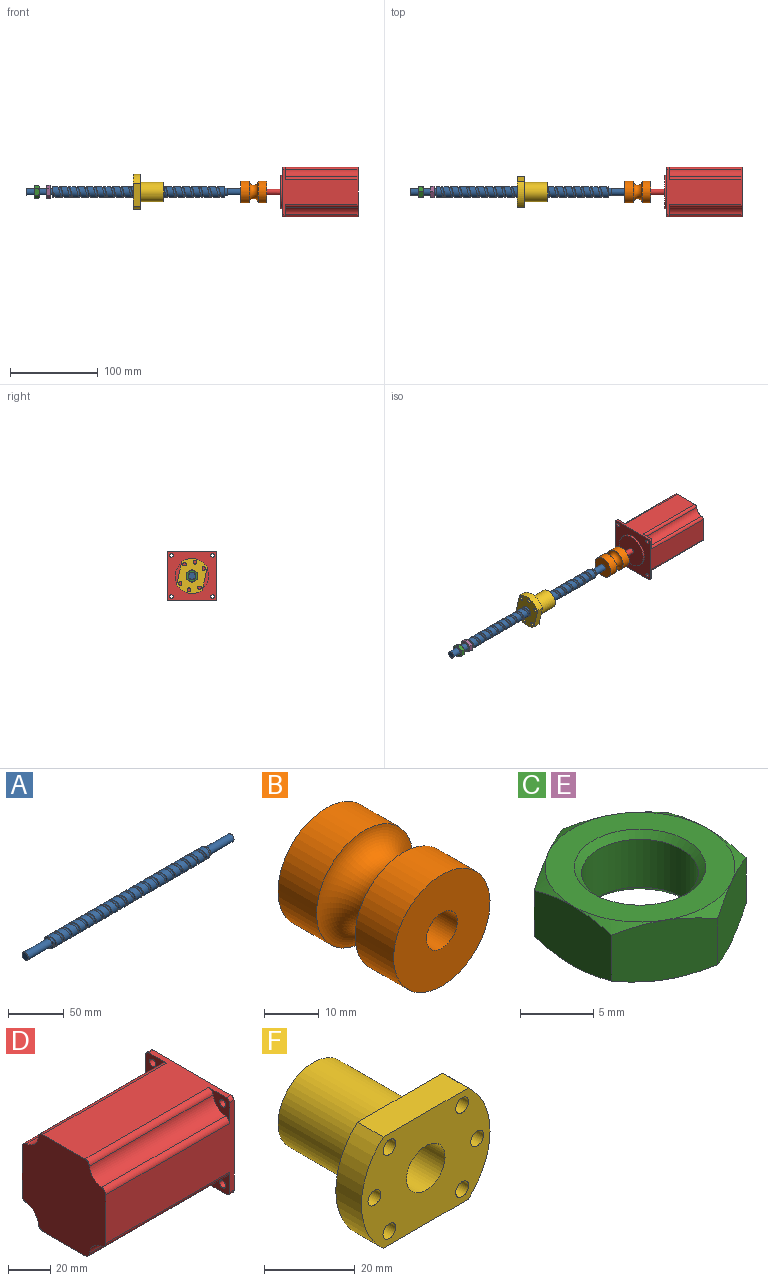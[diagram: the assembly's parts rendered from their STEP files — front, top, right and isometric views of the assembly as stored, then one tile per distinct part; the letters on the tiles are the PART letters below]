
ASSEMBLY  parts=6 mates=5
PART A: 11 faces, bbox 260x18x18 mm
  f0: bspline ~201.75x18mm, area 3000.8mm2, adj f1,f2,f3,f6
  f1: cylinder r=6mm len=197mm, axis (-1,0,0), area 4787.5mm2, adj f0,f2,f3,f6
  f2: plane 1.5x1.5mm, normal (0,-1,0), area 1.8mm2, adj f0,f1,f3
  f3: plane 12x12mm, normal (-1,0,0), area 56.9mm2, adj f0,f1,f2,f4
  f4: cylinder r=4mm len=30mm, axis (1,0,0), area 754mm2, adj f3,f5
  f5: plane 8x8mm, normal (-1,0,0), area 50.3mm2, adj f4
  f6: plane 12x10.87mm, normal (1,0,0), area 39.7mm2, adj f0,f1,f7
  f7: cylinder r=4.42mm len=8.85mm, axis (1,0,0), area 83.4mm2, adj f6,f10
  f8: plane 8x8mm, normal (1,0,0), area 50.3mm2, adj f9
  f9: cylinder r=4mm len=30mm, axis (-1,0,0), area 754mm2, adj f8,f10
  f10: plane 8.85x8.85mm, normal (1,0,0), area 11.2mm2, adj f7,f9
PART B: 8 faces, bbox 34.7x30x34.7 mm
  f0: cylinder r=3.17mm len=8mm, axis (0,-1,0), area 159.6mm2, adj f1,f7
  f1: plane 25x25mm, normal (0,1,0), area 459.2mm2, adj f0,f2
  f2: cylinder r=12.5mm len=25mm, axis (0,-1,0), area 785.4mm2, adj f1,f3
  f3: torus R=12.5mm, axis (0,-1,0), area 919.5mm2, adj f2,f4
  f4: cylinder r=12.5mm len=25mm, axis (0,-1,0), area 785.4mm2, adj f3,f5
  f5: plane 25x25mm, normal (0,-1,0), area 440.6mm2, adj f4,f6
  f6: cylinder r=4mm len=22mm, axis (0,-1,0), area 552.9mm2, adj f5,f7
  f7: plane 8x8mm, normal (0,-1,0), area 18.6mm2, adj f0,f6
PART C: 23 faces, bbox 15.6x15.6x5.6 mm
  f0: plane 7.12x5.63mm, normal (0.5,-0.87,0), area 34.5mm2, adj f1,f5,f6,f7,f8,f9
  f1: plane 7.12x5.63mm, normal (-0.5,-0.87,0), area 34.5mm2, adj f0,f2,f7,f9,f10,f11
  f2: plane 8.13x5.62mm, normal (-1,0,0), area 34.5mm2, adj f1,f3,f10,f11,f12,f13
  f3: plane 7.12x5.63mm, normal (-0.5,0.87,0), area 34.5mm2, adj f2,f4,f12,f13,f14,f15
  f4: plane 7.12x5.63mm, normal (0.5,0.87,0), area 34.5mm2, adj f3,f5,f14,f15,f16,f17
  f5: plane 8.13x5.62mm, normal (1,0,0), area 34.5mm2, adj f0,f4,f6,f8,f16,f17
  f6: cone r=6.5mm half-angle=60deg, axis (0,0,1), area 4.2mm2, adj f0,f5,f19
  f7: cone r=6.5mm half-angle=60deg, axis (0,0,1), area 4.2mm2, adj f0,f1,f19
  f8: cone r=6.5mm half-angle=60deg, axis (0,0,-1), area 4.2mm2, adj f0,f5,f18
  f9: cone r=6.5mm half-angle=60deg, axis (0,0,-1), area 4.2mm2, adj f0,f1,f18
  f10: cone r=6.5mm half-angle=60deg, axis (0,0,1), area 4.2mm2, adj f1,f2,f19
  f11: cone r=6.5mm half-angle=60deg, axis (0,0,-1), area 4.2mm2, adj f1,f2,f18
  f12: cone r=6.5mm half-angle=60deg, axis (0,0,1), area 4.2mm2, adj f2,f3,f19
  f13: cone r=6.5mm half-angle=60deg, axis (0,0,-1), area 4.2mm2, adj f2,f3,f18
  f14: cone r=6.5mm half-angle=60deg, axis (0,0,1), area 4.2mm2, adj f3,f4,f19
  f15: cone r=6.5mm half-angle=60deg, axis (0,0,-1), area 4.2mm2, adj f3,f4,f18
  f16: cone r=6.5mm half-angle=60deg, axis (0,0,1), area 4.2mm2, adj f4,f5,f19
  f17: cone r=6.5mm half-angle=60deg, axis (0,0,-1), area 4.2mm2, adj f4,f5,f18
  f18: plane 13x13mm, normal (0,0,1), area 69.1mm2, adj f8,f9,f11,f13,f15,f17,f21
  f19: plane 13x13mm, normal (0,0,-1), area 69.1mm2, adj f6,f7,f10,f12,f14,f16,f22
  f20: cylinder r=4mm len=8mm, axis (0,0,1), area 100.5mm2, adj f21,f22
  f21: cone r=4mm half-angle=45deg, axis (0,0,1), area 18.9mm2, adj f18,f20
  f22: cone r=4.5mm half-angle=45deg, axis (0,0,-1), area 18.9mm2, adj f19,f20
PART D: 35 faces, bbox 109x56.2x56.2 mm
  f0: plane 56.2x56.2mm, normal (-1,0,0), area 2729.4mm2, adj f2,f4,f6,f9,f20,f22,f23,f26
  f1: cylinder r=2mm len=3mm, axis (-1,0,0), area 9.4mm2, adj f2,f9,f13,f19
  f2: plane 86x52.2mm, normal (0,0,-1), area 2504.1mm2, adj f0,f1,f3,f13,f19,f25,f29,f31
  f3: cylinder r=2mm len=3mm, axis (-1,0,0), area 9.4mm2, adj f2,f4,f13,f25
  f4: plane 86x52.2mm, normal (0,1,0), area 2504.1mm2, adj f0,f3,f5,f13,f21,f25,f27,f32
  f5: cylinder r=2mm len=3mm, axis (-1,0,0), area 9.4mm2, adj f4,f6,f13,f21
  f6: plane 86x52.2mm, normal (0,0,1), area 2504.1mm2, adj f0,f5,f7,f13,f21,f24,f28,f33
  f7: cylinder r=2mm len=3mm, axis (-1,0,0), area 9.4mm2, adj f6,f9,f13,f24
  f8: cylinder r=2mm len=4mm, axis (-1,0,0), area 37.7mm2, adj f13,f25
  f9: plane 86x52.2mm, normal (0,-1,0), area 2504.1mm2, adj f0,f1,f7,f13,f19,f24,f30,f34
  f10: cylinder r=2mm len=4mm, axis (-1,0,0), area 37.7mm2, adj f13,f24
  f11: cylinder r=2mm len=4mm, axis (-1,0,0), area 37.7mm2, adj f13,f21
  f12: cylinder r=2mm len=4mm, axis (-1,0,0), area 37.7mm2, adj f13,f19
  f13: plane 56.2x56.2mm, normal (1,0,0), area 1970.6mm2, adj f1,f2,f3,f4,f5,f6,f7,f8
  f14: cylinder r=19mm len=38mm, axis (-1,0,0), area 238.8mm2, adj f13,f15
  f15: plane 38x38mm, normal (1,0,0), area 1102.4mm2, adj f14,f16
  f16: cylinder r=3.17mm len=20.5mm, axis (-1,0,0), area 409mm2, adj f15,f18
  f17: plane 5.35x5.35mm, normal (1,0,0), area 22.5mm2, adj f18
  f18: torus R=2.67mm, axis (1,0,0), area 14.8mm2, adj f16,f17
  f19: plane 13.96x13.96mm, normal (-1,0,0), area 93.8mm2, adj f1,f2,f9,f12,f20,f29,f30
  f20: cylinder r=9mm len=83mm, axis (1,0,0), area 1048.7mm2, adj f0,f19,f29,f30
  f21: plane 13.96x13.96mm, normal (-1,0,0), area 93.8mm2, adj f4,f5,f6,f11,f22,f27,f28
  f22: cylinder r=9mm len=83mm, axis (1,0,0), area 1048.7mm2, adj f0,f21,f27,f28
  f23: cylinder r=9mm len=83mm, axis (1,0,0), area 1048.7mm2, adj f0,f24,f33,f34
  f24: plane 13.96x13.96mm, normal (-1,0,0), area 93.8mm2, adj f6,f7,f9,f10,f23,f33,f34
  f25: plane 13.96x13.96mm, normal (-1,0,0), area 93.8mm2, adj f2,f3,f4,f8,f26,f31,f32
  f26: cylinder r=9mm len=83mm, axis (1,0,0), area 1048.7mm2, adj f0,f25,f31,f32
  f27: cylinder r=3mm len=83mm, axis (1,0,0), area 370.4mm2, adj f0,f4,f21,f22
  f28: cylinder r=3mm len=83mm, axis (1,0,0), area 370.4mm2, adj f0,f6,f21,f22
  f29: cylinder r=3mm len=83mm, axis (1,0,0), area 370.4mm2, adj f0,f2,f19,f20
  f30: cylinder r=3mm len=83mm, axis (1,0,0), area 370.4mm2, adj f0,f9,f19,f20
  f31: cylinder r=3mm len=83mm, axis (1,0,0), area 370.4mm2, adj f0,f2,f25,f26
  f32: cylinder r=3mm len=83mm, axis (1,0,0), area 370.4mm2, adj f0,f4,f25,f26
  f33: cylinder r=3mm len=83mm, axis (1,0,0), area 370.4mm2, adj f0,f6,f23,f24
  f34: cylinder r=3mm len=83mm, axis (1,0,0), area 370.4mm2, adj f0,f9,f23,f24
PART E: same geometry as C
PART F: 15 faces, bbox 40x35x30 mm
  f0: plane 26.46x8mm, normal (0,0,-1), area 211.7mm2, adj f1,f6,f11,f12
  f1: cylinder r=20mm len=30mm, axis (0,1,0), area 271.4mm2, adj f0,f2,f11,f12
  f2: plane 26.46x8mm, normal (0,0,1), area 211.7mm2, adj f1,f6,f11,f12
  f3: cylinder r=2mm len=8mm, axis (0,1,0), area 100.5mm2, adj f11,f12
  f4: cylinder r=2mm len=8mm, axis (0,1,0), area 100.5mm2, adj f11,f12
  f5: cylinder r=2mm len=8mm, axis (0,1,0), area 100.5mm2, adj f11,f12
  f6: cylinder r=20mm len=30mm, axis (0,1,0), area 271.4mm2, adj f0,f2,f11,f12
  f7: cylinder r=2mm len=8mm, axis (0,1,0), area 100.5mm2, adj f11,f12
  f8: cylinder r=2mm len=8mm, axis (0,1,0), area 100.5mm2, adj f11,f12
  f9: cylinder r=6mm len=35mm, axis (0,1,0), area 1319.5mm2, adj f11,f14
  f10: cylinder r=2mm len=8mm, axis (0,1,0), area 100.5mm2, adj f11,f12
  f11: plane 40x30mm, normal (0,-1,0), area 886.8mm2, adj f0,f1,f2,f3,f4,f5,f6,f7
  f12: plane 40x30mm, normal (0,1,0), area 619.8mm2, adj f0,f1,f2,f3,f4,f5,f6,f7
  f13: cylinder r=11mm len=27mm, axis (0,-1,0), area 1866.1mm2, adj f12,f14
  f14: plane 22x22mm, normal (0,1,0), area 267mm2, adj f9,f13
PLACE A rot(axis=(1,0,0),90deg) t=(-98.41,2.59,-76.23)mm
PLACE B rot(axis=(0.71,0.71,0),180deg) t=(146.59,2.59,-76.23)mm
PLACE C rot(axis=(0.58,0.58,0.58),120deg) t=(-113.41,2.59,-76.23)mm
PLACE D rot(axis=(0,1,0),180deg) t=(250.59,2.59,-76.23)mm fixed
PLACE E rot(axis=(0.58,0.58,0.58),120deg) t=(-100.41,2.59,-76.23)mm
PLACE F rot(axis=(0.62,0.62,-0.49),127.6deg) t=(1.73,2.59,-76.23)mm
MATE fastened C.f6 <-> A.f1  axis (-1,0,0) through (-113.41,2.59,-76.23)mm
MATE cylindrical F.f1 <-> A.f1  axis (1,0,0) through (-6.27,2.59,-76.23)mm
MATE fastened B.f0 <-> A.f1  axis (-1,0,0) through (116.59,2.59,-76.23)mm
MATE fastened E.f6 <-> A.f1  axis (-1,0,0) through (-100.41,2.59,-76.23)mm
MATE fastened D.f14 <-> B.f0  axis (-1,0,0) through (141.59,2.59,-76.23)mm
